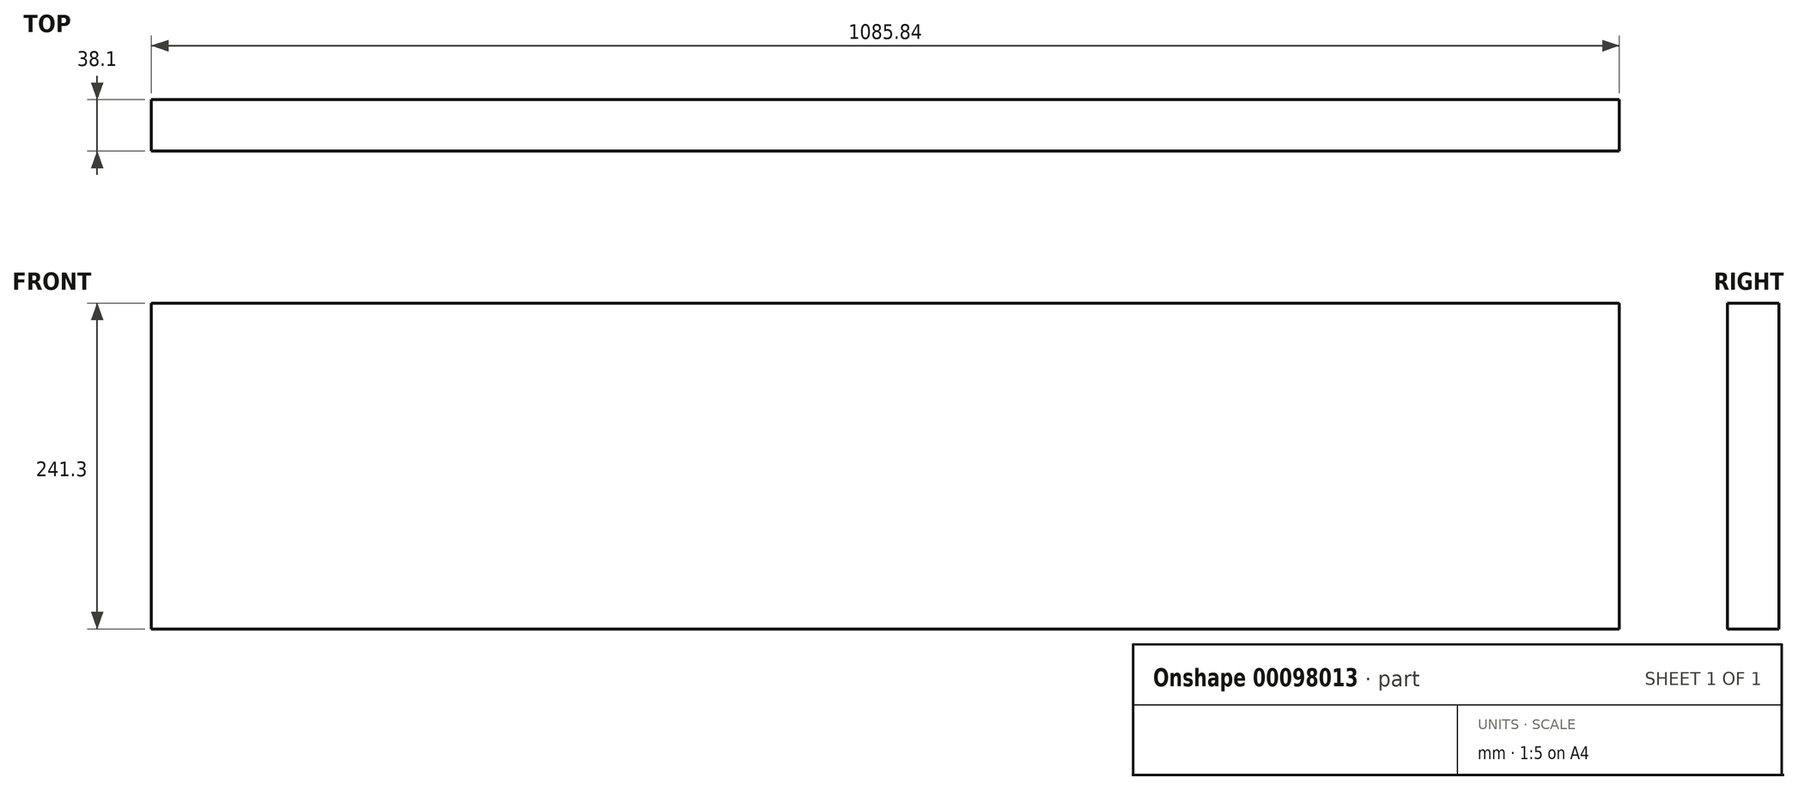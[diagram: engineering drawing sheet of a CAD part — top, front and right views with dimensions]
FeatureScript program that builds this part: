
annotation { "Feature Type Name" : "Feature", "Feature Type Description" : "" }
export const myFeature = defineFeature(function(context is Context, id is Id, definition is map)
    precondition{}
    {
        {
            var Q0;
            Q0=qCreatedBy(makeId("Front.planeOp"),FACE);
            var sketch = newSketch(context, id + "F0", { "sketchPlane" : qUnion([Q0])});
            skLineSegment(sketch, "E0.bottom", {"start": v(542.93, 120.65) * mm, "end": v(-542.93, 120.65) * mm});
            skLineSegment(sketch, "E0.top", {"start": v(542.93, -120.65) * mm, "end": v(-542.93, -120.65) * mm});
            skLineSegment(sketch, "E0.left", {"start": v(542.93, 120.65) * mm, "end": v(542.93, -120.65) * mm});
            skLineSegment(sketch, "E0.right", {"start": v(-542.93, 120.65) * mm, "end": v(-542.93, -120.65) * mm});
            skPoint(sketch, "E0.middle", {"position": v(0, 0) * mm});
            skSolve(sketch);
        }
        {
            var Q0;
            Q0=makeQuery(id+"F0.imprint","IMPRINT",FACE,{"disambiguationData":[TD([[makeQuery(id+"F0.imprint","IMPRINT",EDGE,{"derivedFrom":sQuery(id+"F0.wireOp",EDGE,"E0.bottom")}),1.0]])]});
            extrude(context, id + "F1", {"entities" : qUnion([Q0]), "depth" : 38.1 * mm});
        }
    });
